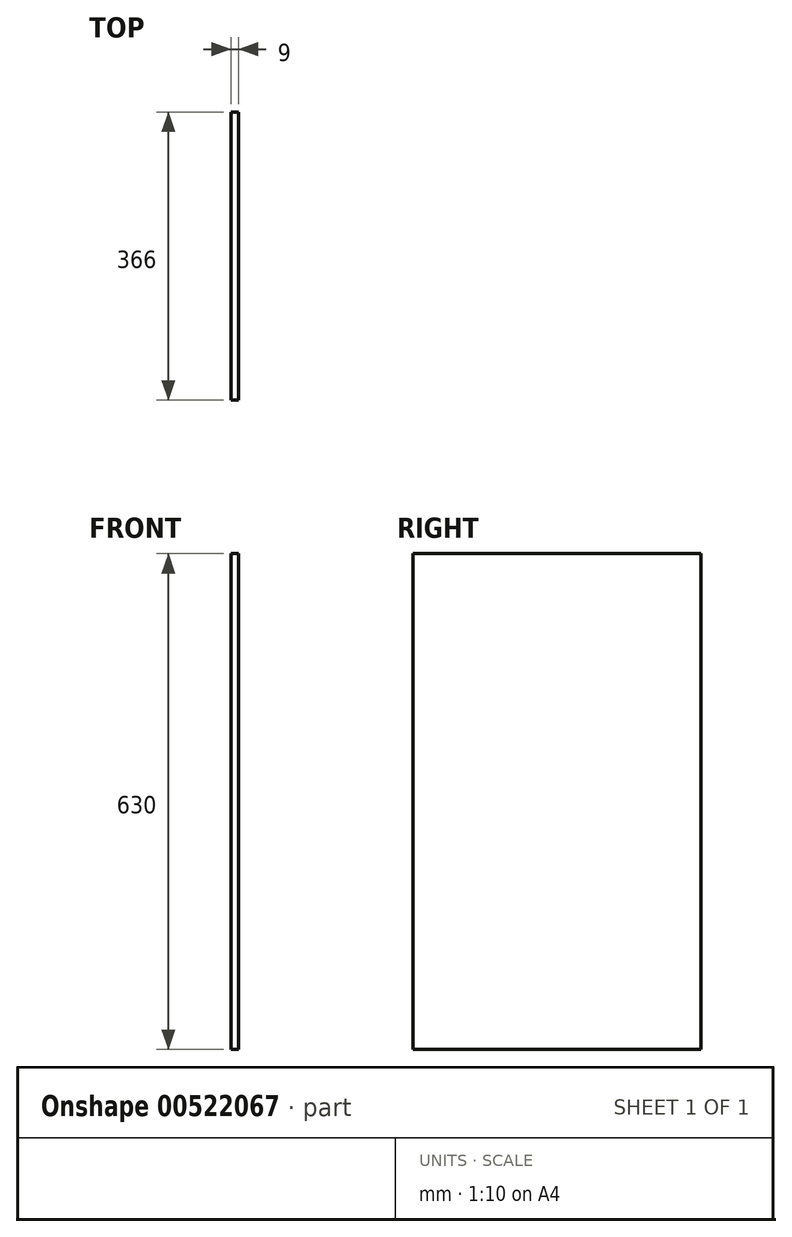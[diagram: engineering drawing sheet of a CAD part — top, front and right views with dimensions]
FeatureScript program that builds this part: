
annotation { "Feature Type Name" : "Feature", "Feature Type Description" : "" }
export const myFeature = defineFeature(function(context is Context, id is Id, definition is map)
    precondition{}
    {
        {
            var Q0;
            Q0=qCreatedBy(makeId("Right.planeOp"),FACE);
            var sketch = newSketch(context, id + "F0", { "sketchPlane" : qUnion([Q0])});
            skLineSegment(sketch, "E0", {"start": v(-366, 0) * mm, "end": v(0, 0) * mm});
            skLineSegment(sketch, "E1", {"start": v(0, 0) * mm, "end": v(0, 630) * mm});
            skLineSegment(sketch, "E2", {"start": v(0, 630) * mm, "end": v(-366, 630) * mm});
            skLineSegment(sketch, "E3", {"start": v(-366, 630) * mm, "end": v(-366, 0) * mm});
            skSolve(sketch);
        }
        {
            var Q0;
            Q0=makeQuery(id+"F0.imprint","IMPRINT",FACE,{"disambiguationData":[TD([[makeQuery(id+"F0.imprint","IMPRINT",EDGE,{"derivedFrom":sQuery(id+"F0.wireOp",EDGE,"E0")}),1.0]])]});
            extrude(context, id + "F1", {"entities" : qUnion([Q0]), "depth" : 9 * mm, "offsetDistance" : 25 * mm});
        }
    });
